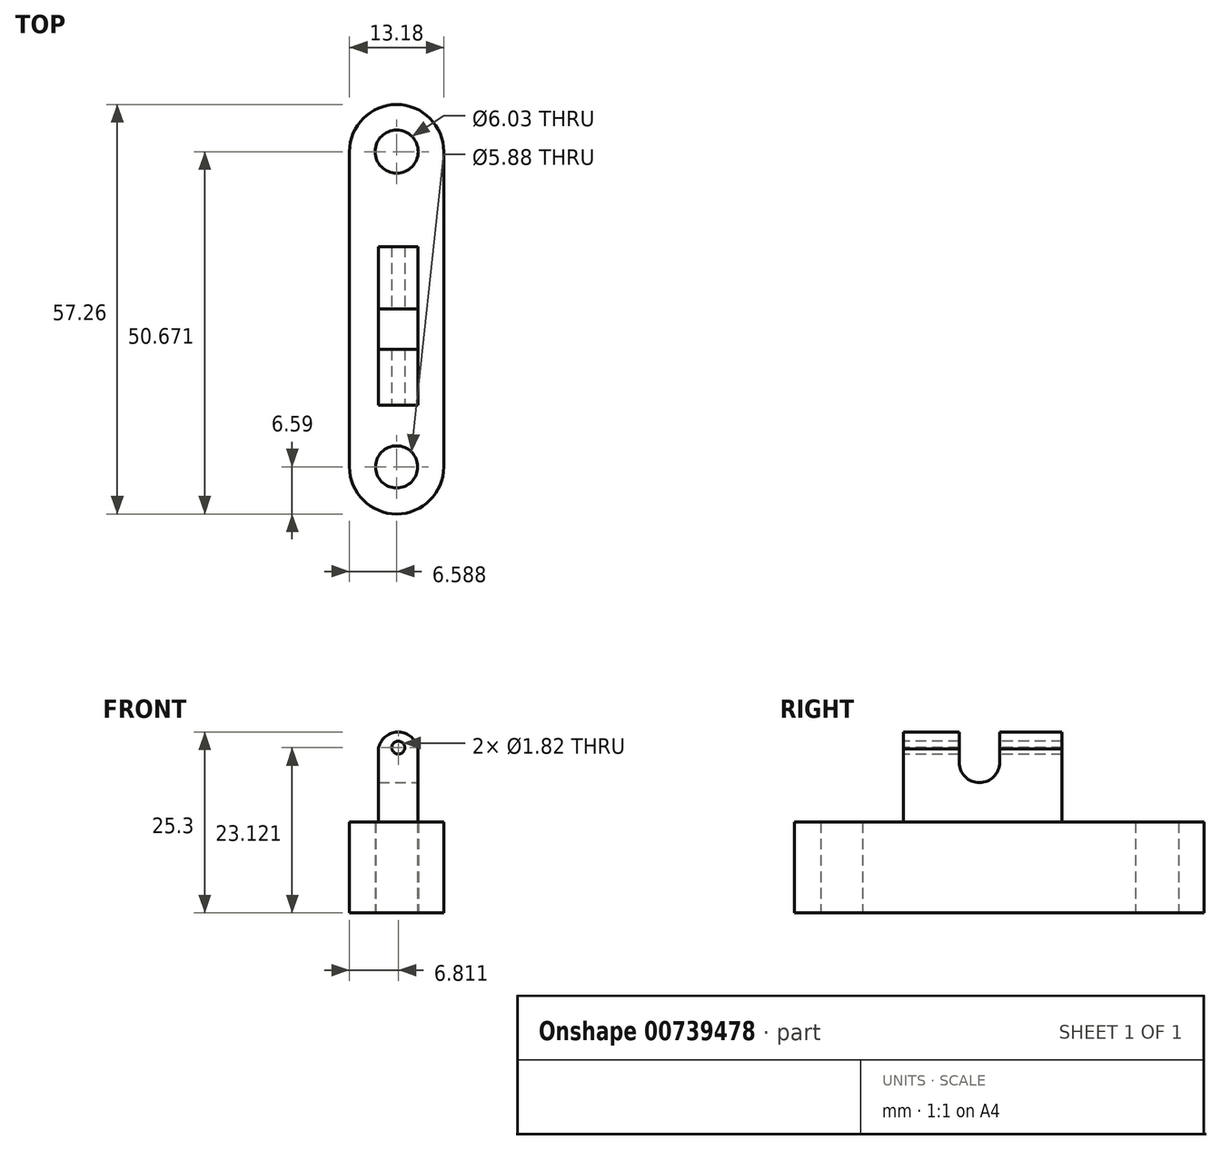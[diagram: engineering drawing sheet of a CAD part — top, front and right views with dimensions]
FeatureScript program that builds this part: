
annotation { "Feature Type Name" : "Feature", "Feature Type Description" : "" }
export const myFeature = defineFeature(function(context is Context, id is Id, definition is map)
    precondition{}
    {
        {
            var Q0;
            Q0=qCreatedBy(makeId("Top.planeOp"),FACE);
            var sketch = newSketch(context, id + "F0", { "sketchPlane" : qUnion([Q0])});
            skLineSegment(sketch, "E0.left", {"start": v(0, 0) * mm, "end": v(0, 44.08) * mm});
            skLineSegment(sketch, "E0.right", {"start": v(13.18, 0) * mm, "end": v(13.18, 44.08) * mm});
            skArc(sketch, "E1", {"start": v(13.18, 44.08) * mm, "mid": v(6.59, 50.67) * mm, "end": v(0, 44.08) * mm});
            skArc(sketch, "E2", {"start": v(0, 0) * mm, "mid": v(6.59, -6.59) * mm, "end": v(13.18, 0) * mm});
            skCircle(sketch, "E3", {"center": v(6.59, 44.08) * mm, "radius": 3.01 * mm});
            skCircle(sketch, "E4", {"center": v(6.59, 0) * mm, "radius": 2.94 * mm});
            skSolve(sketch);
        }
        {
            var Q0;
            Q0=makeQuery(id+"F0.imprint","IMPRINT",FACE,{"disambiguationData":[TD([[makeQuery(id+"F0.imprint","IMPRINT",EDGE,{"derivedFrom":sQuery(id+"F0.wireOp",EDGE,"E0.left")}),-1.0]])]});
            extrude(context, id + "F1", {"entities" : qUnion([Q0]), "depth" : 12.7 * mm, "offsetDistance" : 25.4 * mm});
        }
        {
            var Q0;
            Q0=qCreatedBy(makeId("Top.planeOp"),FACE);
            var sketch = newSketch(context, id + "F2", { "sketchPlane" : qUnion([Q0])});
            skLineSegment(sketch, "E5.bottom", {"start": v(4.08, 30.8) * mm, "end": v(9.57, 30.8) * mm});
            skLineSegment(sketch, "E5.top", {"start": v(4.08, 8.63) * mm, "end": v(9.57, 8.63) * mm});
            skLineSegment(sketch, "E5.left", {"start": v(4.08, 30.8) * mm, "end": v(4.08, 8.63) * mm});
            skLineSegment(sketch, "E5.right", {"start": v(9.57, 30.8) * mm, "end": v(9.57, 8.63) * mm});
            skSolve(sketch);
        }
        {
            var Q0;
            Q0 = qSketchRegion(id + "F2", true);
            extrude(context, id + "F3", {"entities" : qUnion([Q0]), "operationType" : NewBodyOperationType.ADD, "depth" : 25.4 * mm, "offsetDistance" : 25.4 * mm});
        }
        {
            var Q0;
            Q0=makeQuery(id+"F3.opExtrude","SWEPT_FACE",FACE,{"disambiguationData":[OSD([sQuery(id+"F2.wireOp",EDGE,"E5.right")])]});
            var sketch = newSketch(context, id + "F4", { "sketchPlane" : qUnion([Q0])});
            skLineSegment(sketch, "E6.bottom", {"start": v(16.42, 25.4) * mm, "end": v(22.09, 25.4) * mm});
            skLineSegment(sketch, "E6.left", {"start": v(16.42, 25.4) * mm, "end": v(16.42, 21.07) * mm});
            skLineSegment(sketch, "E6.right", {"start": v(22.09, 25.4) * mm, "end": v(22.09, 21.07) * mm});
            skArc(sketch, "E7", {"start": v(16.42, 21.07) * mm, "mid": v(19.25, 18.24) * mm, "end": v(22.09, 21.07) * mm});
            skSolve(sketch);
        }
        {
            var Q0;
            Q0=makeQuery(id+"F4.imprint","IMPRINT",FACE,{"disambiguationData":[TD([[makeQuery(id+"F4.imprint","IMPRINT",EDGE,{"derivedFrom":sQuery(id+"F4.wireOp",EDGE,"E6.left")}),1.0]])]});
            extrude(context, id + "F5", {"entities" : qUnion([Q0]), "operationType" : NewBodyOperationType.REMOVE, "oppositeDirection" : true, "depth" : 25.4 * mm, "offsetDistance" : 25.4 * mm});
        }
        {
            var Q0;
            Q0=makeQuery(id+"F3.opExtrude","SWEPT_FACE",FACE,{"disambiguationData":[OSD([sQuery(id+"F2.wireOp",EDGE,"E5.top")])]});
            var sketch = newSketch(context, id + "F6", { "sketchPlane" : qUnion([Q0])});
            skArc(sketch, "E8", {"start": v(9.57, 22.05) * mm, "mid": v(6.69, 25.3) * mm, "end": v(4.08, 21.82) * mm});
            skLineSegment(sketch, "E9", {"start": v(4.08, 23.17) * mm, "end": v(4.08, 25.4) * mm});
            skLineSegment(sketch, "E10", {"start": v(4.08, 25.4) * mm, "end": v(9.57, 25.4) * mm});
            skLineSegment(sketch, "E11", {"start": v(9.57, 25.4) * mm, "end": v(9.57, 22.94) * mm});
            skLineSegment(sketch, "E12", {"start": v(9.57, 22.94) * mm, "end": v(9.57, 25.4) * mm});
            skLineSegment(sketch, "E13", {"start": v(4.08, 23.17) * mm, "end": v(4.08, 23.54) * mm});
            skLineSegment(sketch, "E14", {"start": v(5.47, 25.4) * mm, "end": v(8.01, 25.4) * mm});
            skSolve(sketch);
        }
        {
            var Q0;
            {var subQ3=sQuery(id+"F6.wireOp",EDGE,"E9");Q0=makeQuery(id+"F6.imprint","IMPRINT",FACE,{"disambiguationData":[TD([[makeQuery(id+"F6.imprint","IMPRINT",EDGE,{"derivedFrom":subQ3}),1.0]])]});}
            extrude(context, id + "F7", {"entities" : qUnion([Q0]), "operationType" : NewBodyOperationType.REMOVE, "oppositeDirection" : true, "depth" : 127 * mm, "offsetDistance" : 25.4 * mm});
        }
        {
            var Q0;
            Q0=makeQuery(id+"F3.opExtrude","SWEPT_FACE",FACE,{"disambiguationData":[OSD([sQuery(id+"F2.wireOp",EDGE,"E5.top")])]});
            var sketch = newSketch(context, id + "F8", { "sketchPlane" : qUnion([Q0])});
            skCircle(sketch, "E15", {"center": v(6.81, 23.12) * mm, "radius": 0.9 * mm});
            skSolve(sketch);
        }
        {
            var Q0;
            Q0=makeQuery(id+"F8.imprint","IMPRINT",FACE,{"disambiguationData":[TD([[makeQuery(id+"F8.imprint","IMPRINT",EDGE,{"derivedFrom":sQuery(id+"F8.wireOp",EDGE,"E15")}),1.0]])]});
            extrude(context, id + "F9", {"entities" : qUnion([Q0]), "operationType" : NewBodyOperationType.REMOVE, "oppositeDirection" : true, "depth" : 127 * mm, "offsetDistance" : 25.4 * mm});
        }
    });
